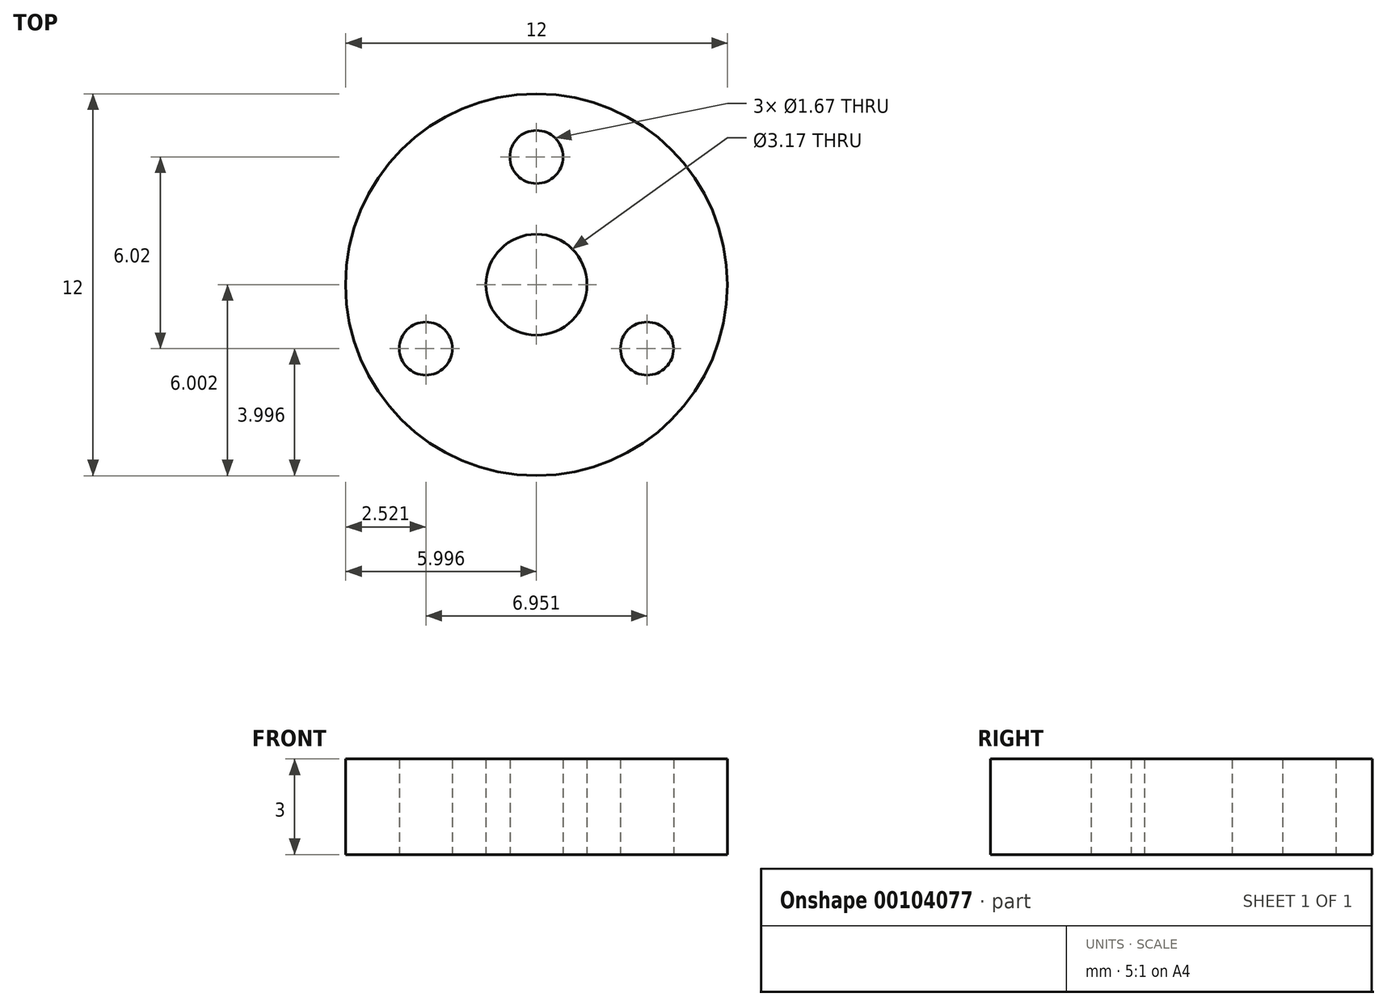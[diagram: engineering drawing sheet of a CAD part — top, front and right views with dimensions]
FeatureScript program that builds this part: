
annotation { "Feature Type Name" : "Feature", "Feature Type Description" : "" }
export const myFeature = defineFeature(function(context is Context, id is Id, definition is map)
    precondition{}
    {
        {
            var Q0;
            Q0=qCreatedBy(makeId("Top.planeOp"),FACE);
            var sketch = newSketch(context, id + "F0", { "sketchPlane" : qUnion([Q0])});
            skCircle(sketch, "E0", {"center": v(-48.13, 13.43) * mm, "radius": 1.59 * mm});
            skCircle(sketch, "E1", {"center": v(-48.13, 13.43) * mm, "radius": 6 * mm});
            skCircle(sketch, "E2", {"center": v(-48.13, 17.45) * mm, "radius": 0.84 * mm});
            skCircle(sketch, "E3.1.0", {"center": v(-51.6, 11.43) * mm, "radius": 0.84 * mm});
            skCircle(sketch, "E3.2.0", {"center": v(-44.66, 11.43) * mm, "radius": 0.84 * mm});
            skSolve(sketch);
        }
        {
            var Q0;
            Q0=makeQuery(id+"F0.imprint","IMPRINT",FACE,{"disambiguationData":[TD([[makeQuery(id+"F0.imprint","IMPRINT",EDGE,{"derivedFrom":sQuery(id+"F0.wireOp",EDGE,"E0")}),-1.0]])]});
            extrude(context, id + "F1", {"entities" : qUnion([Q0]), "depth" : 3 * mm});
        }
    });
